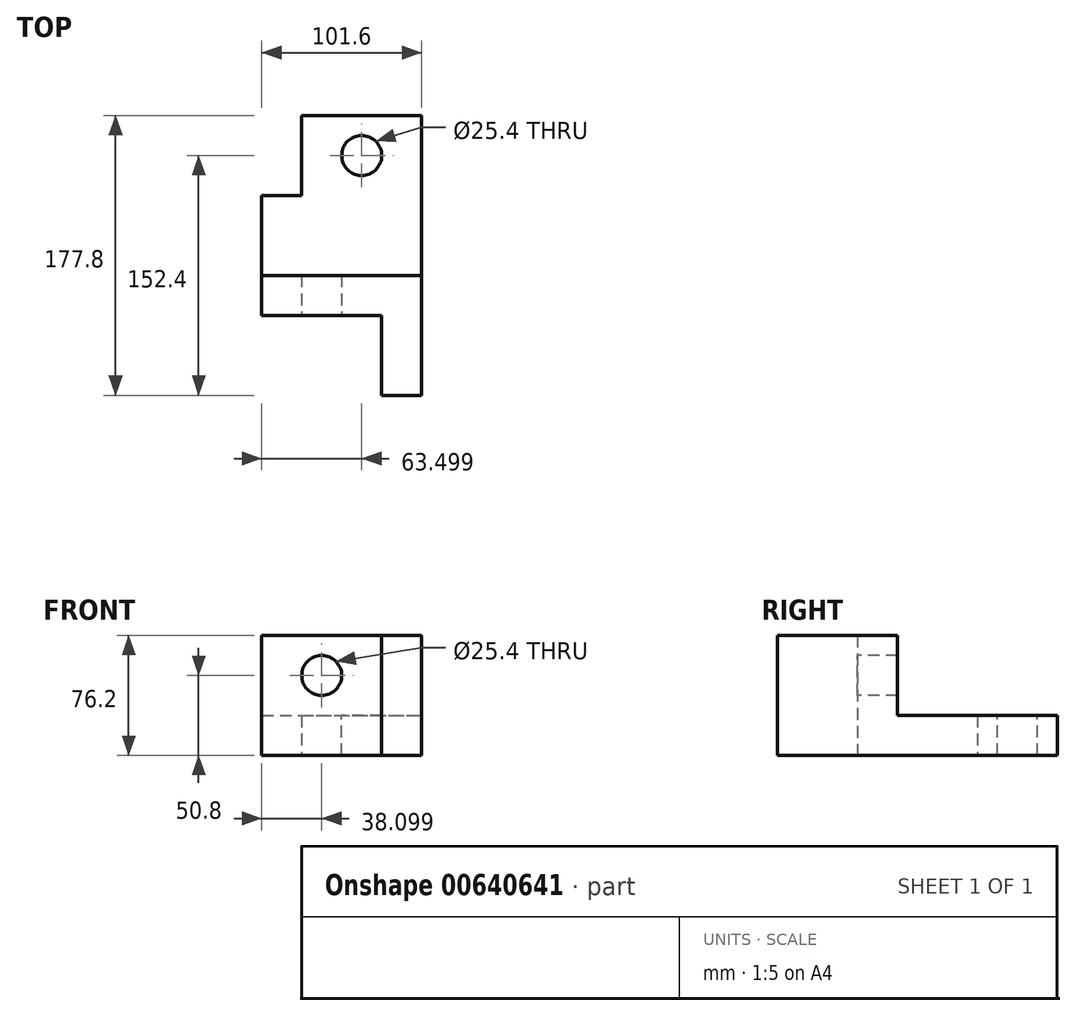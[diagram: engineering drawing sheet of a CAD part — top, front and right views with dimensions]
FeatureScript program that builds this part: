
annotation { "Feature Type Name" : "Feature", "Feature Type Description" : "" }
export const myFeature = defineFeature(function(context is Context, id is Id, definition is map)
    precondition{}
    {
        {
            var Q0;
            Q0=qCreatedBy(makeId("Top.planeOp"),FACE);
            var sketch = newSketch(context, id + "F0", { "sketchPlane" : qUnion([Q0])});
            skLineSegment(sketch, "E0.bottom", {"start": v(3.57, 66.82) * mm, "end": v(79.77, 66.82) * mm});
            skLineSegment(sketch, "E0.top", {"start": v(54.37, -110.98) * mm, "end": v(79.77, -110.98) * mm});
            skLineSegment(sketch, "E0.left", {"start": v(-21.83, 16.02) * mm, "end": v(-21.83, -60.18) * mm});
            skLineSegment(sketch, "E0.right", {"start": v(79.77, 66.82) * mm, "end": v(79.77, -110.98) * mm});
            skLineSegment(sketch, "E1", {"start": v(-21.83, 16.02) * mm, "end": v(3.57, 16.02) * mm});
            skLineSegment(sketch, "E2", {"start": v(3.57, 16.02) * mm, "end": v(3.57, 66.82) * mm});
            skLineSegment(sketch, "E3", {"start": v(-21.83, -60.18) * mm, "end": v(54.37, -60.18) * mm});
            skLineSegment(sketch, "E4", {"start": v(54.37, -60.18) * mm, "end": v(54.37, -110.98) * mm});
            skPoint(sketch, "E5.orphan", {"position": v(-21.83, 66.82) * mm});
            skLineSegment(sketch, "E6", {"start": v(-21.83, -60.18) * mm, "end": v(-21.83, -34.78) * mm});
            skLineSegment(sketch, "E7", {"start": v(-21.83, -34.78) * mm, "end": v(79.77, -34.78) * mm});
            skSolve(sketch);
        }
        {
            var Q0;
            {var subQ1=sQuery(id+"F0.wireOp",EDGE,"E0.bottom");Q0=makeQuery(id+"F0.imprint","IMPRINT",FACE,{"disambiguationData":[TD([[makeQuery(id+"F0.imprint","IMPRINT",EDGE,{"derivedFrom":subQ1}),-1.0]])]});}
            extrude(context, id + "F1", {"entities" : qUnion([Q0]), "depth" : 25.4 * mm, "offsetDistance" : 25.4 * mm});
        }
        {
            var Q0;
            {var subQ1=sQuery(id+"F0.wireOp",EDGE,"E0.top");Q0=makeQuery(id+"F0.imprint","IMPRINT",FACE,{"disambiguationData":[TD([[makeQuery(id+"F0.imprint","IMPRINT",EDGE,{"derivedFrom":subQ1}),1.0]])]});}
            extrude(context, id + "F2", {"entities" : qUnion([Q0]), "operationType" : NewBodyOperationType.ADD, "depth" : 76.2 * mm, "offsetDistance" : 25.4 * mm});
        }
        {
            var Q0;
            Q0=makeQuery(id+"F2.opExtrude","SWEPT_FACE",FACE,{"disambiguationData":[OSD([sQuery(id+"F0.wireOp",EDGE,"E3")])]});
            var sketch = newSketch(context, id + "F3", { "sketchPlane" : qUnion([Q0])});
            skLineSegment(sketch, "E8", {"start": v(18.36, 76.2) * mm, "end": v(16.27, 76.2) * mm, "construction": true});
            skLineSegment(sketch, "E9", {"start": v(16.27, 76.2) * mm, "end": v(16.27, 50.8) * mm, "construction": true});
            skCircle(sketch, "E10", {"center": v(16.27, 50.8) * mm, "radius": 12.7 * mm});
            skSolve(sketch);
        }
        {
            var Q0;
            Q0=makeQuery(id+"F3.imprint","IMPRINT",FACE,{"disambiguationData":[TD([[makeQuery(id+"F3.imprint","IMPRINT",EDGE,{"derivedFrom":sQuery(id+"F3.wireOp",EDGE,"E10")}),1.0]])]});
            extrude(context, id + "F4", {"entities" : qUnion([Q0]), "operationType" : NewBodyOperationType.REMOVE, "endBound" : BoundingType.THROUGH_ALL, "oppositeDirection" : true, "depth" : 25.4 * mm, "offsetDistance" : 25.4 * mm});
        }
        {
            var Q0;
            Q0=makeQuery(id+"F1.opExtrude","CAP_FACE",FACE,{"disambiguationData":[OSD([sQuery(id+"F0.wireOp",EDGE,"E0.bottom"),sQuery(id+"F0.wireOp",EDGE,"E0.right"),sQuery(id+"F0.wireOp",EDGE,"E1"),sQuery(id+"F0.wireOp",EDGE,"E2"),sQuery(id+"F0.wireOp",EDGE,"E0.left"),sQuery(id+"F0.wireOp",EDGE,"E7")])],"isStart":false});
            var sketch = newSketch(context, id + "F5", { "sketchPlane" : qUnion([Q0])});
            skLineSegment(sketch, "E11", {"start": v(41.67, 66.82) * mm, "end": v(41.67, 41.42) * mm, "construction": true});
            skCircle(sketch, "E12", {"center": v(41.67, 41.42) * mm, "radius": 12.7 * mm});
            skSolve(sketch);
        }
        {
            var Q0;
            Q0=makeQuery(id+"F5.imprint","IMPRINT",FACE,{"disambiguationData":[TD([[makeQuery(id+"F5.imprint","IMPRINT",EDGE,{"derivedFrom":sQuery(id+"F5.wireOp",EDGE,"E12")}),1.0]])]});
            extrude(context, id + "F6", {"entities" : qUnion([Q0]), "operationType" : NewBodyOperationType.REMOVE, "endBound" : BoundingType.THROUGH_ALL, "oppositeDirection" : true, "depth" : 25.4 * mm, "offsetDistance" : 25.4 * mm});
        }
    });
